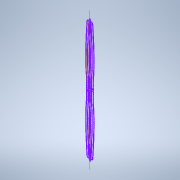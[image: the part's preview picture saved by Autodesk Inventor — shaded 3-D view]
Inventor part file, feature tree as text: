
AUTODESK INVENTOR PART (.ipt)
format: ipt  version: 2022 (Build 260153000, 153)  size: 2,258,432 bytes
history: native  units: mm
features: sketch x6, other x2, sweep x2
ambient origin geometry x8: Origin, YZ Plane, XZ Plane, XY Plane, X Axis, Y Axis, Z Axis, Center Point
bodies: Body1 (feature_tree), Body2 (feature_tree)
feature tree (10):
  sketch  "Sketch1"  dims[d0=380.0mm d1=0.0mm d2=0.0mm]
  sketch  "Sketch4"
  sketch  "Sketch2"  dims[d3=380.0mm d4=90.0deg]
  sketch  "3D Sketch1"
  other  "Srf1"
  sketch  "Sketch3"  dims[d5=0.0mm d6=0.0mm]
  sketch  "3D Sketch2"
  other  "Srf2"
  sweep  "SweepSrf1"
  sweep  "SweepSrf2"
